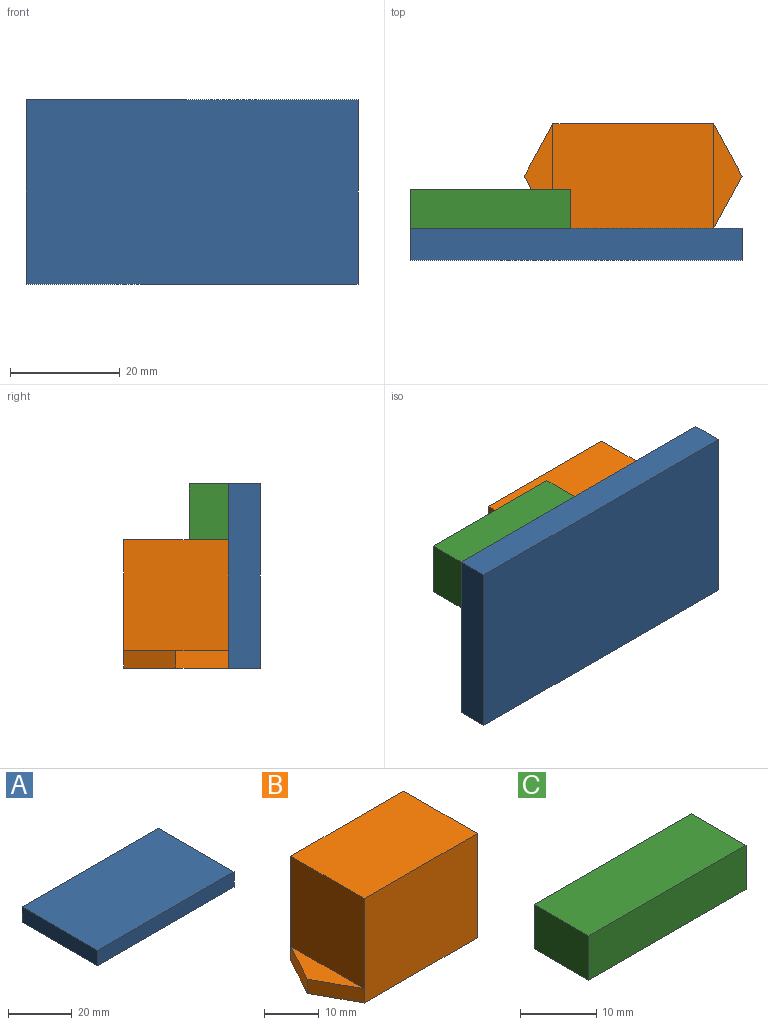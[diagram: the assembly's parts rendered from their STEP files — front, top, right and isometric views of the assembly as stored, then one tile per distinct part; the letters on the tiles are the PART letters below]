
ASSEMBLY  parts=3 mates=6
PART A: 6 faces, bbox 60.5x33.5x5.8 mm
  f0: plane 60.45x5.84mm, normal (0,1,0), area 353.2mm2, adj f1,f3,f4,f5
  f1: plane 33.53x5.84mm, normal (-1,0,0), area 195.9mm2, adj f0,f2,f4,f5
  f2: plane 60.45x5.84mm, normal (0,-1,0), area 353.2mm2, adj f1,f3,f4,f5
  f3: plane 33.53x5.84mm, normal (1,0,0), area 195.9mm2, adj f0,f2,f4,f5
  f4: plane 60.45x33.53mm, normal (0,0,1), area 2026.8mm2, adj f0,f1,f2,f3
  f5: plane 60.45x33.53mm, normal (0,0,-1), area 2026.8mm2, adj f0,f1,f2,f3
PART B: 12 faces, bbox 39.6x19.1x23.4 mm
  f0: plane 29.21x23.37mm, normal (0,1,0), area 682.6mm2, adj f1,f3,f4,f5,f6,f9
  f1: plane 20.19x19.05mm, normal (-1,0,0), area 384.7mm2, adj f0,f2,f4,f8
  f2: plane 29.21x23.37mm, normal (0,-1,0), area 682.6mm2, adj f1,f3,f4,f5,f7,f10
  f3: plane 20.19x19.05mm, normal (1,0,0), area 384.7mm2, adj f0,f2,f4,f11
  f4: plane 29.21x19.05mm, normal (0,0,1), area 556.5mm2, adj f0,f1,f2,f3
  f5: plane 39.62x19.05mm, normal (0,0,-1), area 655.6mm2, adj f0,f2,f6,f7,f9,f10
  f6: plane 9.53x5.21mm, normal (-0.88,0.48,0), area 34.5mm2, adj f0,f5,f7,f8
  f7: plane 9.53x5.21mm, normal (-0.88,-0.48,0), area 34.5mm2, adj f2,f5,f6,f8
  f8: plane 19.05x5.21mm, normal (0,0,1), area 49.6mm2, adj f1,f6,f7
  f9: plane 9.53x5.21mm, normal (0.88,0.48,0), area 34.5mm2, adj f0,f5,f10,f11
  f10: plane 9.53x5.21mm, normal (0.88,-0.48,0), area 34.5mm2, adj f2,f5,f9,f11
  f11: plane 19.05x5.21mm, normal (0,0,1), area 49.6mm2, adj f3,f9,f10
PART C: 6 faces, bbox 29.2x10.2x7.1 mm
  f0: plane 29.21x7.11mm, normal (0,-1,0), area 207.7mm2, adj f1,f3,f4,f5
  f1: plane 10.16x7.11mm, normal (1,0,0), area 72.3mm2, adj f0,f2,f4,f5
  f2: plane 29.21x7.11mm, normal (0,1,0), area 207.7mm2, adj f1,f3,f4,f5
  f3: plane 10.16x7.11mm, normal (-1,0,0), area 72.3mm2, adj f0,f2,f4,f5
  f4: plane 29.21x10.16mm, normal (0,0,1), area 296.8mm2, adj f0,f1,f2,f3
  f5: plane 29.21x10.16mm, normal (0,0,-1), area 296.8mm2, adj f0,f1,f2,f3
PLACE A rot(axis=(0,-0.71,0.71),180deg) t=(-10.41,-9.52,16.76)mm
PLACE B at identity fixed
PLACE C rot(axis=(-1,0,0),90deg) t=(-26.03,-9.52,28.45)mm
MATE planar C.f3 <-> A.f3  axis (-1,0,0) through (-40.64,-5.97,28.45)mm
MATE planar C.f2 <-> B.f4  axis (0,0,-1) through (-26.03,-5.97,23.37)mm
MATE planar A.f5 <-> B.f2  axis (0,1,0) through (-10.41,-9.52,16.76)mm
MATE planar B.f5 <-> A.f0  axis (0,0,-1) through (0,0,0)mm
MATE planar A.f5 <-> C.f5  axis (0,1,0) through (-10.41,-9.52,16.76)mm
MATE planar C.f5 <-> A.f5  axis (0,-1,0) through (-26.03,-9.52,28.45)mm
